# Revit family: Storage-Teknion-PLDWS_Worksurface_Height_Drawer_Cabinet_Standard-R2015
name_source: partatom
category: Furniture
revit_build: Autodesk Revit Architecture 2015 (Build: 20140323_1530(x64)
units: mm (PartAtom-declared; Revit-internal decimal feet)

## types (3) — shared parameters
Assembly Code = E2020200
Bottom of Middle Drawer = 13.156 "
Height = 27.2 "
Manufacturer = Teknion
Manufacturer Fax = 416.661.4586
Part Number = PLDWS
Product Documentation Link = http://www.teknion.com
Product Line = Filing & Storage
Product Page URL = http://www.teknion.com
Series = Ledger Plus
Sustainability Data = http://www.teknion.com
Top of Middle Drawer = 19.426 "
Top of Top Drawer = 25.825 "
URL = www.teknion.com
Unit Weight URL = http://www.teknion.com
Warranty = http://www.teknion.com

## per-type parameters (varying)
| type | Bottom of Bottom Drawer | Bottom of Top Drawer | ConfigurationBBF | ConfigurationBQ | ConfigurationLF | Description | Model | Top of Bottom Drawer |
| Worksurface Height Drawer Cabinet - Standard - Configuration - Box / Box / File | 1.98 " | 19.582 " | Yes | No | No | Worksurface Height Drawer Cabinet -  Box / Box / File | PLDWS_BBF_ | 13 " |
| Worksurface Height Drawer Cabinet - Standard - Configuration - Box / Extra Large File | 1.515 " | 17.506 " | No | Yes | No | Worksurface Height Drawer Cabinet - Box / Extra Large File | PLDWS_BQ_ | 17.35 " |
| Worksurface Height Drawer Cabinet - Standard - Configuration - Large File / File | 1.98 " | 13.156 " | No | No | Yes | Worksurface Height Drawer Cabinet -  Large File / File | PLDWS_LF_ | 13 " |

## geometry (parser evidence)
native form markers: Sweep x2
no freeform markers — native parametric forms only
